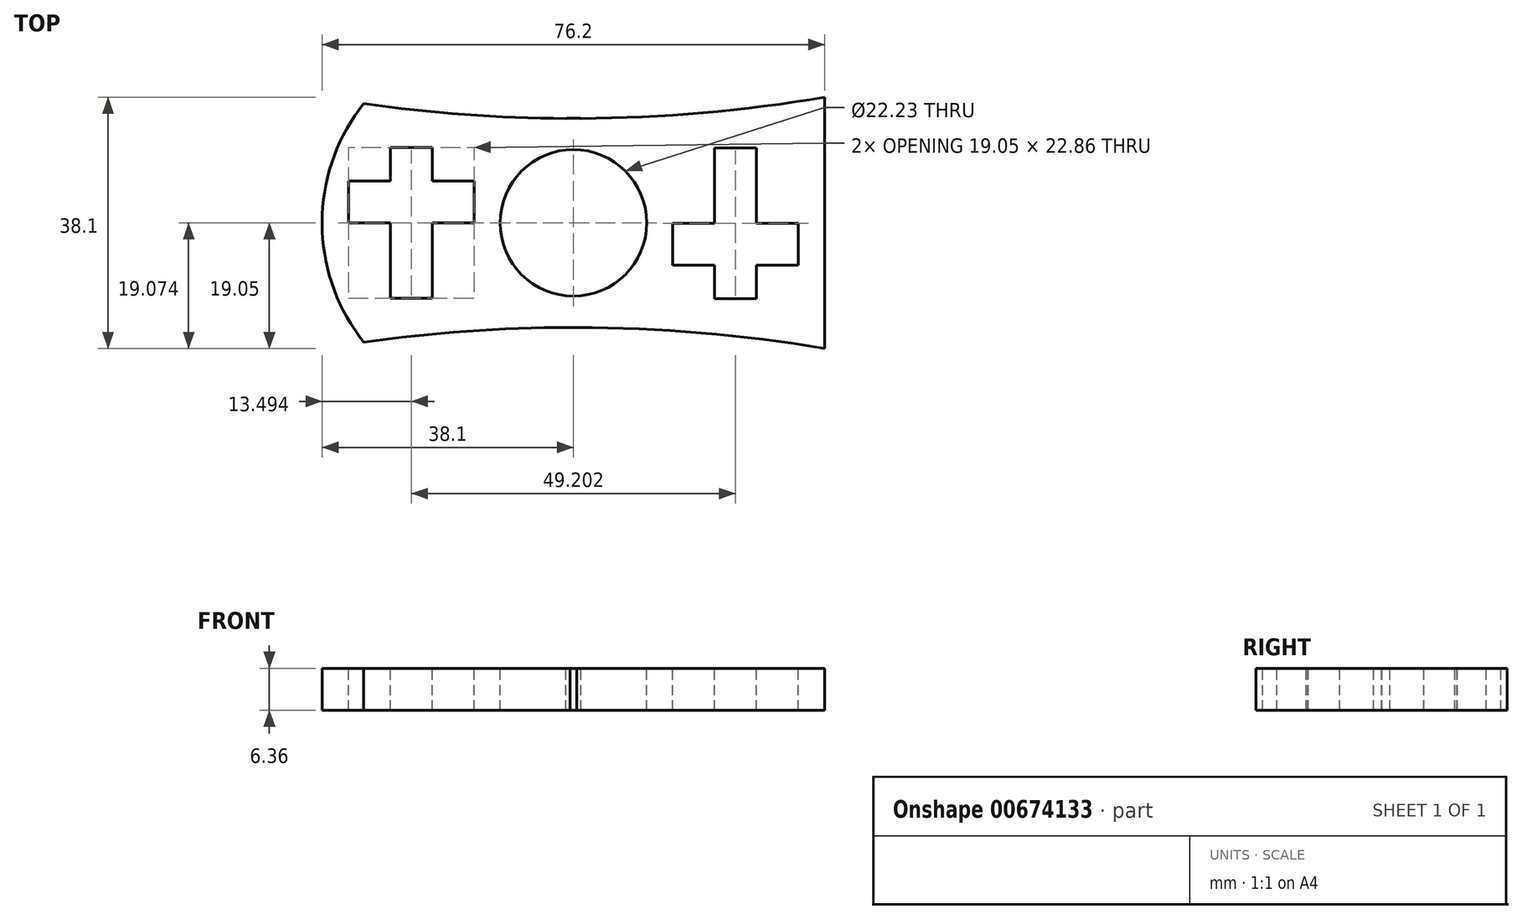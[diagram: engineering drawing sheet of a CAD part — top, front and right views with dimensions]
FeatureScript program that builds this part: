
annotation { "Feature Type Name" : "Feature", "Feature Type Description" : "" }
export const myFeature = defineFeature(function(context is Context, id is Id, definition is map)
    precondition{}
    {
        {
            var Q0;
            Q0=qCreatedBy(makeId("Top.planeOp"),FACE);
            var sketch = newSketch(context, id + "F0", { "sketchPlane" : qUnion([Q0])});
            skLineSegment(sketch, "E0.bottom", {"start": v(38.1, 38.1) * mm, "end": v(-38.1, 38.1) * mm});
            skLineSegment(sketch, "E0.top", {"start": v(38.1, -38.1) * mm, "end": v(-38.1, -38.1) * mm});
            skLineSegment(sketch, "E0.left", {"start": v(38.1, 38.1) * mm, "end": v(38.1, -38.1) * mm});
            skLineSegment(sketch, "E0.right", {"start": v(-38.1, 38.1) * mm, "end": v(-38.1, -38.1) * mm});
            skPoint(sketch, "E0.middle", {"position": v(0, 0) * mm});
            skSolve(sketch);
        }
        {
            var Q0;
            Q0 = qSketchRegion(id + "F0", true);
            extrude(context, id + "F1", {"entities" : qUnion([Q0]), "depth" : 3.17 * mm, "offsetDistance" : 25.4 * mm, "hasSecondDirection" : true, "secondDirectionOppositeDirection" : true, "secondDirectionDepth" : 3.17 * mm});
        }
        {
            var Q0;
            Q0=makeQuery(id+"F1.opExtrude","CAP_FACE",FACE,{"disambiguationData":[OSD([sQuery(id+"F0.wireOp",EDGE,"E0.bottom"),sQuery(id+"F0.wireOp",EDGE,"E0.top"),sQuery(id+"F0.wireOp",EDGE,"E0.left"),sQuery(id+"F0.wireOp",EDGE,"E0.right")])],"isStart":false});
            var sketch = newSketch(context, id + "F2", { "sketchPlane" : qUnion([Q0])});
            skCircle(sketch, "E1", {"center": v(0, 0) * mm, "radius": 11.11 * mm});
            skSolve(sketch);
        }
        {
            var Q0;
            Q0 = qSketchRegion(id + "F2", true);
            extrude(context, id + "F3", {"entities" : qUnion([Q0]), "operationType" : NewBodyOperationType.REMOVE, "oppositeDirection" : true, "depth" : 25.4 * mm, "offsetDistance" : 25.4 * mm});
        }
        {
            var Q0;
            Q0=makeQuery(id+"F1.opExtrude","CAP_FACE",FACE,{"disambiguationData":[OSD([sQuery(id+"F0.wireOp",EDGE,"E0.bottom"),sQuery(id+"F0.wireOp",EDGE,"E0.top"),sQuery(id+"F0.wireOp",EDGE,"E0.left"),sQuery(id+"F0.wireOp",EDGE,"E0.right")])],"isStart":false});
            var sketch = newSketch(context, id + "F4", { "sketchPlane" : qUnion([Q0])});
            skCircle(sketch, "E2", {"center": v(0, 0) * mm, "radius": 15.88 * mm});
            skLineSegment(sketch, "E3", {"start": v(-38.1, 38.1) * mm, "end": v(-38.1, 19.05) * mm});
            skLineSegment(sketch, "E4", {"start": v(38.1, 38.1) * mm, "end": v(38.1, 19.05) * mm});
            skArc(sketch, "E5", {"start": v(-38.1, 19.05) * mm, "mid": v(0, 15.83) * mm, "end": v(38.1, 19.05) * mm});
            skLineSegment(sketch, "E6", {"start": v(-38.1, -38.1) * mm, "end": v(-38.1, -19.05) * mm});
            skLineSegment(sketch, "E7", {"start": v(38.1, -38.1) * mm, "end": v(38.1, -19.05) * mm});
            skArc(sketch, "E8", {"start": v(38.1, -19.05) * mm, "mid": v(0, -15.87) * mm, "end": v(-38.1, -19.05) * mm});
            skSolve(sketch);
        }
        {
            var Q0;
            {var subQ1=sQuery(id+"F4.wireOp",EDGE,"E3");Q0=makeQuery(id+"F4.imprint","IMPRINT",FACE,{"disambiguationData":[TD([[makeQuery(id+"F4.imprint","IMPRINT",EDGE,{"derivedFrom":subQ1}),1.0]])]});}
            var Q1;
            {var subQ4=sQuery(id+"F4.wireOp",EDGE,"E6");Q1=makeQuery(id+"F4.imprint","IMPRINT",FACE,{"disambiguationData":[TD([[makeQuery(id+"F4.imprint","IMPRINT",EDGE,{"derivedFrom":subQ4}),1.0]])]});}
            extrude(context, id + "F5", {"entities" : qUnion([Q0, Q1]), "operationType" : NewBodyOperationType.REMOVE, "oppositeDirection" : true, "depth" : 25.4 * mm, "offsetDistance" : 25.4 * mm});
        }
        {
            var Q0;
            Q0=makeQuery(id+"F1.opExtrude","CAP_FACE",FACE,{"disambiguationData":[OSD([sQuery(id+"F0.wireOp",EDGE,"E0.bottom"),sQuery(id+"F0.wireOp",EDGE,"E0.top"),sQuery(id+"F0.wireOp",EDGE,"E0.left"),sQuery(id+"F0.wireOp",EDGE,"E0.right")])],"isStart":false});
            var sketch = newSketch(context, id + "F6", { "sketchPlane" : qUnion([Q0])});
            skLineSegment(sketch, "E9", {"start": v(38.1, 19.05) * mm, "end": v(31.83, 18.07) * mm});
            skLineSegment(sketch, "E10", {"start": v(38.1, -19.05) * mm, "end": v(31.82, -18.08) * mm});
            skArc(sketch, "E11", {"start": v(31.82, -18.08) * mm, "mid": v(38.1, 0) * mm, "end": v(31.83, 18.07) * mm});
            skLineSegment(sketch, "E12", {"start": v(-38.1, 19.05) * mm, "end": v(-31.83, 18.07) * mm});
            skLineSegment(sketch, "E13", {"start": v(-38.1, -19.05) * mm, "end": v(-31.82, -18.08) * mm});
            skArc(sketch, "E14", {"start": v(-31.83, 18.07) * mm, "mid": v(-38.13, 0) * mm, "end": v(-31.82, -18.08) * mm});
            skSolve(sketch);
        }
        {
            var Q0;
            {var subQ0=sQuery(id+"F6.wireOp",EDGE,"E14");var subQ3=makeQuery(id+"F1.opExtrude","CAP_EDGE",EDGE,{"disambiguationData":[OSD([sQuery(id+"F0.wireOp",EDGE,"E0.right")])],"isStart":false});var subQ6=subQ3;var subQ7=makeQuery(id+"F6.imprint","INTERSECT",VERTEX,{"disambiguationData":[OD(1.0)],"derivedFrom":[subQ6,subQ0]});Q0=makeQuery(id+"F6.imprint","IMPRINT",FACE,{"disambiguationData":[TD([[makeQuery(id+"F6.imprint","IMPRINT",EDGE,{"disambiguationData":[TD([[subQ7,-1.0]])],"derivedFrom":subQ0}),-1.0]])]});}
            var Q1;
            {var subQ0=sQuery(id+"F6.wireOp",EDGE,"E11");var subQ3=makeQuery(id+"F1.opExtrude","CAP_EDGE",EDGE,{"disambiguationData":[OSD([sQuery(id+"F0.wireOp",EDGE,"E0.left")])],"isStart":false});var subQ6=subQ3;var subQ7=makeQuery(id+"F6.imprint","INTERSECT",VERTEX,{"disambiguationData":[OD(0.0)],"derivedFrom":[subQ6,subQ0]});Q1=makeQuery(id+"F6.imprint","IMPRINT",FACE,{"disambiguationData":[TD([[makeQuery(id+"F6.imprint","IMPRINT",EDGE,{"disambiguationData":[TD([[subQ7,1.0]])],"derivedFrom":subQ0}),-1.0]])]});}
            var Q2;
            {var subQ0=sQuery(id+"F6.wireOp",EDGE,"E11");var subQ3=makeQuery(id+"F1.opExtrude","CAP_EDGE",EDGE,{"disambiguationData":[OSD([sQuery(id+"F0.wireOp",EDGE,"E0.left")])],"isStart":false});var subQ6=subQ3;var subQ7=makeQuery(id+"F6.imprint","INTERSECT",VERTEX,{"disambiguationData":[OD(1.0)],"derivedFrom":[subQ6,subQ0]});Q2=makeQuery(id+"F6.imprint","IMPRINT",FACE,{"disambiguationData":[TD([[makeQuery(id+"F6.imprint","IMPRINT",EDGE,{"disambiguationData":[TD([[subQ7,-1.0]])],"derivedFrom":subQ0}),-1.0]])]});}
            var Q3;
            {var subQ0=sQuery(id+"F6.wireOp",EDGE,"E14");var subQ3=makeQuery(id+"F1.opExtrude","CAP_EDGE",EDGE,{"disambiguationData":[OSD([sQuery(id+"F0.wireOp",EDGE,"E0.right")])],"isStart":false});var subQ6=subQ3;var subQ7=makeQuery(id+"F6.imprint","INTERSECT",VERTEX,{"disambiguationData":[OD(0.0)],"derivedFrom":[subQ6,subQ0]});Q3=makeQuery(id+"F6.imprint","IMPRINT",FACE,{"disambiguationData":[TD([[makeQuery(id+"F6.imprint","IMPRINT",EDGE,{"disambiguationData":[TD([[subQ7,1.0]])],"derivedFrom":subQ0}),-1.0]])]});}
            extrude(context, id + "F7", {"entities" : qUnion([Q0, Q1, Q2, Q3]), "operationType" : NewBodyOperationType.REMOVE, "oppositeDirection" : true, "depth" : 25.4 * mm, "offsetDistance" : 25.4 * mm});
        }
        {
            var Q0;
            Q0=makeQuery(id+"F1.opExtrude","CAP_FACE",FACE,{"disambiguationData":[OSD([sQuery(id+"F0.wireOp",EDGE,"E0.bottom"),sQuery(id+"F0.wireOp",EDGE,"E0.top"),sQuery(id+"F0.wireOp",EDGE,"E0.left"),sQuery(id+"F0.wireOp",EDGE,"E0.right")])],"isStart":false});
            var sketch = newSketch(context, id + "F8", { "sketchPlane" : qUnion([Q0])});
            skLineSegment(sketch, "E15", {"start": v(-24.6, 11.45) * mm, "end": v(-21.43, 11.45) * mm});
            skLineSegment(sketch, "E16", {"start": v(-21.43, 11.45) * mm, "end": v(-27.78, 11.45) * mm});
            skLineSegment(sketch, "E17", {"start": v(-27.78, 11.45) * mm, "end": v(-27.78, 6.37) * mm});
            skLineSegment(sketch, "E18", {"start": v(-27.78, 6.37) * mm, "end": v(-34.13, 6.37) * mm});
            skLineSegment(sketch, "E19", {"start": v(-21.43, 11.45) * mm, "end": v(-21.43, 6.37) * mm});
            skLineSegment(sketch, "E20", {"start": v(-21.43, 6.37) * mm, "end": v(-15.08, 6.37) * mm});
            skLineSegment(sketch, "E21", {"start": v(-15.08, 6.37) * mm, "end": v(-15.08, 0.02) * mm});
            skLineSegment(sketch, "E22", {"start": v(-15.08, 0.02) * mm, "end": v(-21.43, 0.02) * mm});
            skLineSegment(sketch, "E23", {"start": v(-21.43, 0.02) * mm, "end": v(-21.43, -11.4) * mm});
            skLineSegment(sketch, "E24", {"start": v(-21.43, -11.4) * mm, "end": v(-27.78, -11.4) * mm});
            skLineSegment(sketch, "E25", {"start": v(-27.78, -11.4) * mm, "end": v(-27.78, 0.02) * mm});
            skLineSegment(sketch, "E26", {"start": v(-27.78, 0.02) * mm, "end": v(-34.13, 0.02) * mm});
            skLineSegment(sketch, "E27", {"start": v(-34.13, 0.02) * mm, "end": v(-34.13, 6.37) * mm});
            skLineSegment(sketch, "E28", {"start": v(24.56, -11.47) * mm, "end": v(27.77, -11.47) * mm});
            skLineSegment(sketch, "E29", {"start": v(27.77, -11.47) * mm, "end": v(21.42, -11.47) * mm});
            skLineSegment(sketch, "E30", {"start": v(21.42, -11.47) * mm, "end": v(21.42, -6.4) * mm});
            skLineSegment(sketch, "E31", {"start": v(21.42, -6.4) * mm, "end": v(15.07, -6.4) * mm});
            skLineSegment(sketch, "E32", {"start": v(15.07, -6.4) * mm, "end": v(15.07, -0.04) * mm});
            skLineSegment(sketch, "E33", {"start": v(15.07, -0.04) * mm, "end": v(21.42, -0.04) * mm});
            skLineSegment(sketch, "E34", {"start": v(21.42, -0.04) * mm, "end": v(21.42, 11.39) * mm});
            skLineSegment(sketch, "E35", {"start": v(21.42, 11.39) * mm, "end": v(27.77, 11.39) * mm});
            skLineSegment(sketch, "E36", {"start": v(27.77, 11.39) * mm, "end": v(27.77, -0.04) * mm});
            skLineSegment(sketch, "E37", {"start": v(27.77, -0.04) * mm, "end": v(34.12, -0.04) * mm});
            skLineSegment(sketch, "E38", {"start": v(34.12, -0.04) * mm, "end": v(34.12, -6.4) * mm});
            skLineSegment(sketch, "E39", {"start": v(34.12, -6.4) * mm, "end": v(27.77, -6.4) * mm});
            skLineSegment(sketch, "E40", {"start": v(27.77, -6.4) * mm, "end": v(27.77, -11.47) * mm});
            skSolve(sketch);
        }
        {
            var Q0;
            Q0 = qSketchRegion(id + "F8", true);
            extrude(context, id + "F9", {"entities" : qUnion([Q0]), "operationType" : NewBodyOperationType.REMOVE, "oppositeDirection" : true, "depth" : 25.4 * mm, "offsetDistance" : 25.4 * mm});
        }
        {
            var Q0;
            Q0 = qSketchRegion(id + "F8", true);
            extrude(context, id + "F10", {"entities" : qUnion([Q0]), "operationType" : NewBodyOperationType.REMOVE, "oppositeDirection" : true, "depth" : 25.4 * mm, "offsetDistance" : 25.4 * mm});
        }
    });
